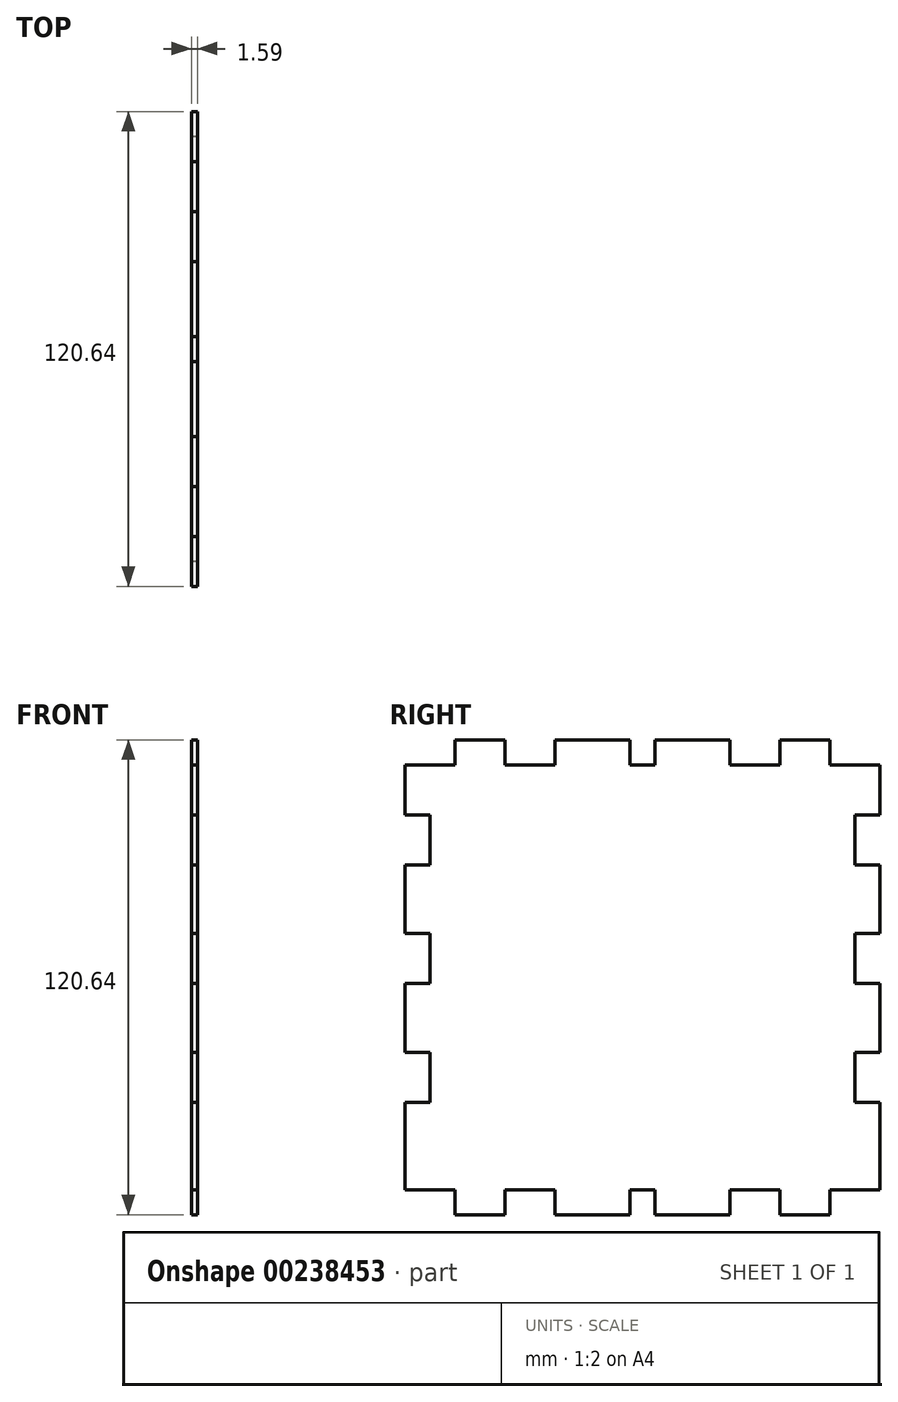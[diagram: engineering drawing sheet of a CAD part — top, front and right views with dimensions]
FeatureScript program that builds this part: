
annotation { "Feature Type Name" : "Feature", "Feature Type Description" : "" }
export const myFeature = defineFeature(function(context is Context, id is Id, definition is map)
    precondition{}
    {
        {
            var Q0;
            Q0=qCreatedBy(makeId("Right.planeOp"),FACE);
            var sketch = newSketch(context, id + "F0", { "sketchPlane" : qUnion([Q0])});
            skLineSegment(sketch, "E0.bottom", {"start": v(60.32, 60.33) * mm, "end": v(-60.33, 60.33) * mm});
            skLineSegment(sketch, "E0.top", {"start": v(60.33, -60.33) * mm, "end": v(-60.32, -60.33) * mm});
            skLineSegment(sketch, "E0.left", {"start": v(60.32, 60.33) * mm, "end": v(60.33, -60.33) * mm});
            skLineSegment(sketch, "E0.right", {"start": v(-60.33, 60.33) * mm, "end": v(-60.32, -60.33) * mm});
            skPoint(sketch, "E0.middle", {"position": v(0, 0) * mm});
            skSolve(sketch);
        }
        {
            var Q0;
            Q0=makeQuery(id+"F0.imprint","IMPRINT",FACE,{"disambiguationData":[TD([[makeQuery(id+"F0.imprint","IMPRINT",EDGE,{"derivedFrom":sQuery(id+"F0.wireOp",EDGE,"E0.bottom")}),1.0]])]});
            extrude(context, id + "F1", {"entities" : qUnion([Q0]), "depth" : 1.59 * mm});
        }
        {
            var Q0;
            Q0=makeQuery(id+"F1.opExtrude","CAP_FACE",FACE,{"disambiguationData":[OSD([sQuery(id+"F0.wireOp",EDGE,"E0.bottom"),sQuery(id+"F0.wireOp",EDGE,"E0.top"),sQuery(id+"F0.wireOp",EDGE,"E0.left"),sQuery(id+"F0.wireOp",EDGE,"E0.right")])],"isStart":true});
            var sketch = newSketch(context, id + "F2", { "sketchPlane" : qUnion([Q0])});
            skLineSegment(sketch, "E1.bottom", {"start": v(60.33, 60.33) * mm, "end": v(47.63, 60.33) * mm});
            skLineSegment(sketch, "E1.top", {"start": v(60.33, 53.98) * mm, "end": v(47.63, 53.98) * mm});
            skLineSegment(sketch, "E1.left", {"start": v(60.33, 60.33) * mm, "end": v(60.33, 53.98) * mm});
            skLineSegment(sketch, "E1.right", {"start": v(47.63, 60.33) * mm, "end": v(47.63, 53.98) * mm});
            skSolve(sketch);
        }
        {
            var Q0;
            Q0=makeQuery(id+"F2.imprint","IMPRINT",FACE,{"disambiguationData":[TD([[makeQuery(id+"F2.imprint","IMPRINT",EDGE,{"derivedFrom":sQuery(id+"F2.wireOp",EDGE,"E1.bottom")}),-1.0]])]});
            extrude(context, id + "F3", {"entities" : qUnion([Q0]), "operationType" : NewBodyOperationType.REMOVE, "oppositeDirection" : true, "depth" : 1.59 * mm});
        }
        {
            var Q0;
            Q0=makeQuery(id+"F1.opExtrude","CAP_FACE",FACE,{"disambiguationData":[OSD([sQuery(id+"F0.wireOp",EDGE,"E0.bottom"),sQuery(id+"F0.wireOp",EDGE,"E0.top"),sQuery(id+"F0.wireOp",EDGE,"E0.left"),sQuery(id+"F0.wireOp",EDGE,"E0.right")])],"isStart":true});
            var sketch = newSketch(context, id + "F4", { "sketchPlane" : qUnion([Q0])});
            skLineSegment(sketch, "E2.bottom", {"start": v(34.93, 60.33) * mm, "end": v(22.23, 60.33) * mm});
            skLineSegment(sketch, "E2.top", {"start": v(34.93, 53.98) * mm, "end": v(22.23, 53.98) * mm});
            skLineSegment(sketch, "E2.left", {"start": v(34.93, 60.33) * mm, "end": v(34.93, 53.98) * mm});
            skLineSegment(sketch, "E2.right", {"start": v(22.23, 60.33) * mm, "end": v(22.23, 53.98) * mm});
            skSolve(sketch);
        }
        {
            var Q0;
            Q0=qSketchRegion(id+"F4",true);
            extrude(context, id + "F5", {"entities" : qUnion([Q0]), "operationType" : NewBodyOperationType.REMOVE, "oppositeDirection" : true, "depth" : 1.59 * mm});
        }
        {
            var Q0;
            Q0=makeQuery(id+"F1.opExtrude","CAP_FACE",FACE,{"disambiguationData":[OSD([sQuery(id+"F0.wireOp",EDGE,"E0.bottom"),sQuery(id+"F0.wireOp",EDGE,"E0.top"),sQuery(id+"F0.wireOp",EDGE,"E0.left"),sQuery(id+"F0.wireOp",EDGE,"E0.right")])],"isStart":true});
            var sketch = newSketch(context, id + "F6", { "sketchPlane" : qUnion([Q0])});
            skLineSegment(sketch, "E3.bottom", {"start": v(3.18, 60.33) * mm, "end": v(-3.17, 60.33) * mm});
            skLineSegment(sketch, "E3.top", {"start": v(3.18, 53.98) * mm, "end": v(-3.17, 53.98) * mm});
            skLineSegment(sketch, "E3.left", {"start": v(3.18, 60.33) * mm, "end": v(3.18, 53.98) * mm});
            skLineSegment(sketch, "E3.right", {"start": v(-3.17, 60.33) * mm, "end": v(-3.17, 53.98) * mm});
            skSolve(sketch);
        }
        {
            var Q0;
            Q0=qSketchRegion(id+"F6",true);
            extrude(context, id + "F7", {"entities" : qUnion([Q0]), "operationType" : NewBodyOperationType.REMOVE, "oppositeDirection" : true, "depth" : 1.59 * mm});
        }
        {
            var Q0;
            Q0=makeQuery(id+"F1.opExtrude","CAP_FACE",FACE,{"disambiguationData":[OSD([sQuery(id+"F0.wireOp",EDGE,"E0.bottom"),sQuery(id+"F0.wireOp",EDGE,"E0.top"),sQuery(id+"F0.wireOp",EDGE,"E0.left"),sQuery(id+"F0.wireOp",EDGE,"E0.right")])],"isStart":true});
            var sketch = newSketch(context, id + "F8", { "sketchPlane" : qUnion([Q0])});
            skLineSegment(sketch, "E4.bottom", {"start": v(-60.32, 60.33) * mm, "end": v(-47.62, 60.33) * mm});
            skLineSegment(sketch, "E4.top", {"start": v(-60.32, 53.98) * mm, "end": v(-47.62, 53.98) * mm});
            skLineSegment(sketch, "E4.left", {"start": v(-60.32, 60.33) * mm, "end": v(-60.32, 53.98) * mm});
            skLineSegment(sketch, "E4.right", {"start": v(-47.62, 60.33) * mm, "end": v(-47.62, 53.98) * mm});
            skSolve(sketch);
        }
        {
            var Q0;
            Q0=makeQuery(id+"F8.imprint","IMPRINT",FACE,{"disambiguationData":[TD([[makeQuery(id+"F8.imprint","IMPRINT",EDGE,{"derivedFrom":sQuery(id+"F8.wireOp",EDGE,"E4.bottom")}),-1.0]])]});
            extrude(context, id + "F9", {"entities" : qUnion([Q0]), "operationType" : NewBodyOperationType.REMOVE, "oppositeDirection" : true, "depth" : 1.59 * mm});
        }
        {
            var Q0;
            Q0=makeQuery(id+"F1.opExtrude","CAP_FACE",FACE,{"disambiguationData":[OSD([sQuery(id+"F0.wireOp",EDGE,"E0.bottom"),sQuery(id+"F0.wireOp",EDGE,"E0.top"),sQuery(id+"F0.wireOp",EDGE,"E0.left"),sQuery(id+"F0.wireOp",EDGE,"E0.right")])],"isStart":true});
            var sketch = newSketch(context, id + "F10", { "sketchPlane" : qUnion([Q0])});
            skLineSegment(sketch, "E5.bottom", {"start": v(-22.22, 60.33) * mm, "end": v(-34.92, 60.33) * mm});
            skLineSegment(sketch, "E5.top", {"start": v(-22.22, 53.98) * mm, "end": v(-34.92, 53.98) * mm});
            skLineSegment(sketch, "E5.left", {"start": v(-22.22, 60.33) * mm, "end": v(-22.22, 53.98) * mm});
            skLineSegment(sketch, "E5.right", {"start": v(-34.92, 60.33) * mm, "end": v(-34.92, 53.98) * mm});
            skSolve(sketch);
        }
        {
            var Q0;
            Q0=makeQuery(id+"F10.imprint","IMPRINT",FACE,{"disambiguationData":[TD([[makeQuery(id+"F10.imprint","IMPRINT",EDGE,{"derivedFrom":sQuery(id+"F10.wireOp",EDGE,"E5.bottom")}),-1.0]])]});
            extrude(context, id + "F11", {"entities" : qUnion([Q0]), "operationType" : NewBodyOperationType.REMOVE, "oppositeDirection" : true, "depth" : 1.59 * mm});
        }
        {
            var Q0;
            Q0=makeQuery(id+"F1.opExtrude","CAP_FACE",FACE,{"disambiguationData":[OSD([sQuery(id+"F0.wireOp",EDGE,"E0.bottom"),sQuery(id+"F0.wireOp",EDGE,"E0.top"),sQuery(id+"F0.wireOp",EDGE,"E0.left"),sQuery(id+"F0.wireOp",EDGE,"E0.right")])],"isStart":true});
            var sketch = newSketch(context, id + "F12", { "sketchPlane" : qUnion([Q0])});
            skLineSegment(sketch, "E6.bottom", {"start": v(-60.32, 41.28) * mm, "end": v(-53.97, 41.28) * mm});
            skLineSegment(sketch, "E6.top", {"start": v(-60.32, 28.58) * mm, "end": v(-53.97, 28.58) * mm});
            skLineSegment(sketch, "E6.left", {"start": v(-60.32, 41.28) * mm, "end": v(-60.32, 28.57) * mm});
            skLineSegment(sketch, "E6.right", {"start": v(-53.97, 41.28) * mm, "end": v(-53.97, 28.58) * mm});
            skSolve(sketch);
        }
        {
            var Q0;
            Q0=makeQuery(id+"F12.imprint","IMPRINT",FACE,{"disambiguationData":[TD([[makeQuery(id+"F12.imprint","IMPRINT",EDGE,{"derivedFrom":sQuery(id+"F12.wireOp",EDGE,"E6.bottom")}),-1.0]])]});
            extrude(context, id + "F13", {"entities" : qUnion([Q0]), "operationType" : NewBodyOperationType.REMOVE, "oppositeDirection" : true, "depth" : 1.59 * mm});
        }
        {
            var Q0;
            Q0=makeQuery(id+"F1.opExtrude","CAP_FACE",FACE,{"disambiguationData":[OSD([sQuery(id+"F0.wireOp",EDGE,"E0.bottom"),sQuery(id+"F0.wireOp",EDGE,"E0.top"),sQuery(id+"F0.wireOp",EDGE,"E0.left"),sQuery(id+"F0.wireOp",EDGE,"E0.right")])],"isStart":true});
            var sketch = newSketch(context, id + "F14", { "sketchPlane" : qUnion([Q0])});
            skLineSegment(sketch, "E7.bottom", {"start": v(-60.32, 11.11) * mm, "end": v(-53.97, 11.11) * mm});
            skLineSegment(sketch, "E7.top", {"start": v(-60.32, -1.59) * mm, "end": v(-53.97, -1.59) * mm});
            skLineSegment(sketch, "E7.left", {"start": v(-60.32, 11.11) * mm, "end": v(-60.32, -1.59) * mm});
            skLineSegment(sketch, "E7.right", {"start": v(-53.97, 11.11) * mm, "end": v(-53.97, -1.59) * mm});
            skSolve(sketch);
        }
        {
            var Q0;
            Q0=makeQuery(id+"F14.imprint","IMPRINT",FACE,{"disambiguationData":[TD([[makeQuery(id+"F14.imprint","IMPRINT",EDGE,{"derivedFrom":sQuery(id+"F14.wireOp",EDGE,"E7.bottom")}),-1.0]])]});
            extrude(context, id + "F15", {"entities" : qUnion([Q0]), "operationType" : NewBodyOperationType.REMOVE, "oppositeDirection" : true, "depth" : 1.59 * mm});
        }
        {
            var Q0;
            Q0=makeQuery(id+"F1.opExtrude","CAP_FACE",FACE,{"disambiguationData":[OSD([sQuery(id+"F0.wireOp",EDGE,"E0.bottom"),sQuery(id+"F0.wireOp",EDGE,"E0.top"),sQuery(id+"F0.wireOp",EDGE,"E0.left"),sQuery(id+"F0.wireOp",EDGE,"E0.right")])],"isStart":true});
            var sketch = newSketch(context, id + "F16", { "sketchPlane" : qUnion([Q0])});
            skLineSegment(sketch, "E8.bottom", {"start": v(-60.33, -19.05) * mm, "end": v(-53.98, -19.05) * mm});
            skLineSegment(sketch, "E8.top", {"start": v(-60.33, -31.75) * mm, "end": v(-53.98, -31.75) * mm});
            skLineSegment(sketch, "E8.left", {"start": v(-60.33, -19.05) * mm, "end": v(-60.33, -31.75) * mm});
            skLineSegment(sketch, "E8.right", {"start": v(-53.98, -19.05) * mm, "end": v(-53.98, -31.75) * mm});
            skSolve(sketch);
        }
        {
            var Q0;
            Q0=makeQuery(id+"F16.imprint","IMPRINT",FACE,{"disambiguationData":[TD([[makeQuery(id+"F16.imprint","IMPRINT",EDGE,{"derivedFrom":sQuery(id+"F16.wireOp",EDGE,"E8.bottom")}),-1.0]])]});
            extrude(context, id + "F17", {"entities" : qUnion([Q0]), "operationType" : NewBodyOperationType.REMOVE, "oppositeDirection" : true, "depth" : 1.59 * mm});
        }
        {
            var Q0;
            Q0=makeQuery(id+"F1.opExtrude","CAP_FACE",FACE,{"disambiguationData":[OSD([sQuery(id+"F0.wireOp",EDGE,"E0.bottom"),sQuery(id+"F0.wireOp",EDGE,"E0.top"),sQuery(id+"F0.wireOp",EDGE,"E0.left"),sQuery(id+"F0.wireOp",EDGE,"E0.right")])],"isStart":true});
            var sketch = newSketch(context, id + "F18", { "sketchPlane" : qUnion([Q0])});
            skLineSegment(sketch, "E9.bottom", {"start": v(-60.33, -53.98) * mm, "end": v(-47.63, -53.98) * mm});
            skLineSegment(sketch, "E9.top", {"start": v(-60.33, -60.33) * mm, "end": v(-47.63, -60.33) * mm});
            skLineSegment(sketch, "E9.left", {"start": v(-60.33, -53.98) * mm, "end": v(-60.33, -60.33) * mm});
            skLineSegment(sketch, "E9.right", {"start": v(-47.63, -53.98) * mm, "end": v(-47.63, -60.33) * mm});
            skLineSegment(sketch, "E10.bottom", {"start": v(60.32, -53.98) * mm, "end": v(47.62, -53.98) * mm});
            skLineSegment(sketch, "E10.top", {"start": v(60.32, -60.33) * mm, "end": v(47.62, -60.33) * mm});
            skLineSegment(sketch, "E10.left", {"start": v(60.32, -53.98) * mm, "end": v(60.32, -60.33) * mm});
            skLineSegment(sketch, "E10.right", {"start": v(47.62, -53.98) * mm, "end": v(47.62, -60.33) * mm});
            skSolve(sketch);
        }
        {
            var Q0;
            Q0=qSketchRegion(id+"F18",true);
            extrude(context, id + "F19", {"entities" : qUnion([Q0]), "operationType" : NewBodyOperationType.REMOVE, "oppositeDirection" : true, "depth" : 1.59 * mm});
        }
        {
            var Q0;
            Q0=makeQuery(id+"F1.opExtrude","CAP_FACE",FACE,{"disambiguationData":[OSD([sQuery(id+"F0.wireOp",EDGE,"E0.bottom"),sQuery(id+"F0.wireOp",EDGE,"E0.top"),sQuery(id+"F0.wireOp",EDGE,"E0.left"),sQuery(id+"F0.wireOp",EDGE,"E0.right")])],"isStart":true});
            var sketch = newSketch(context, id + "F20", { "sketchPlane" : qUnion([Q0])});
            skLineSegment(sketch, "E11.bottom", {"start": v(-34.93, -60.33) * mm, "end": v(-22.23, -60.33) * mm});
            skLineSegment(sketch, "E11.top", {"start": v(-34.93, -53.98) * mm, "end": v(-22.23, -53.98) * mm});
            skLineSegment(sketch, "E11.left", {"start": v(-34.93, -60.33) * mm, "end": v(-34.93, -53.98) * mm});
            skLineSegment(sketch, "E11.right", {"start": v(-22.23, -60.33) * mm, "end": v(-22.23, -53.98) * mm});
            skLineSegment(sketch, "E12.bottom", {"start": v(-3.18, -60.33) * mm, "end": v(3.17, -60.33) * mm});
            skLineSegment(sketch, "E12.top", {"start": v(-3.18, -53.98) * mm, "end": v(3.17, -53.98) * mm});
            skLineSegment(sketch, "E12.left", {"start": v(-3.18, -60.33) * mm, "end": v(-3.18, -53.98) * mm});
            skLineSegment(sketch, "E12.right", {"start": v(3.17, -60.33) * mm, "end": v(3.17, -53.98) * mm});
            skLineSegment(sketch, "E13.bottom", {"start": v(22.22, -60.33) * mm, "end": v(34.92, -60.33) * mm});
            skLineSegment(sketch, "E13.top", {"start": v(22.22, -53.97) * mm, "end": v(34.92, -53.97) * mm});
            skLineSegment(sketch, "E13.left", {"start": v(22.22, -60.33) * mm, "end": v(22.22, -53.97) * mm});
            skLineSegment(sketch, "E13.right", {"start": v(34.92, -60.33) * mm, "end": v(34.92, -53.97) * mm});
            skSolve(sketch);
        }
        {
            var Q0;
            Q0=qSketchRegion(id+"F20",true);
            extrude(context, id + "F21", {"entities" : qUnion([Q0]), "operationType" : NewBodyOperationType.REMOVE, "oppositeDirection" : true, "depth" : 1.59 * mm});
        }
        {
            var Q0;
            Q0=makeQuery(id+"F1.opExtrude","CAP_FACE",FACE,{"disambiguationData":[OSD([sQuery(id+"F0.wireOp",EDGE,"E0.bottom"),sQuery(id+"F0.wireOp",EDGE,"E0.top"),sQuery(id+"F0.wireOp",EDGE,"E0.left"),sQuery(id+"F0.wireOp",EDGE,"E0.right")])],"isStart":true});
            var sketch = newSketch(context, id + "F22", { "sketchPlane" : qUnion([Q0])});
            skLineSegment(sketch, "E14.bottom", {"start": v(60.33, 41.27) * mm, "end": v(53.98, 41.27) * mm});
            skLineSegment(sketch, "E14.top", {"start": v(60.33, 28.57) * mm, "end": v(53.98, 28.57) * mm});
            skLineSegment(sketch, "E14.left", {"start": v(60.33, 41.27) * mm, "end": v(60.33, 28.57) * mm});
            skLineSegment(sketch, "E14.right", {"start": v(53.98, 41.27) * mm, "end": v(53.98, 28.57) * mm});
            skLineSegment(sketch, "E15.bottom", {"start": v(60.33, 11.11) * mm, "end": v(53.98, 11.11) * mm});
            skLineSegment(sketch, "E15.top", {"start": v(60.33, -1.59) * mm, "end": v(53.98, -1.59) * mm});
            skLineSegment(sketch, "E15.left", {"start": v(60.33, 11.11) * mm, "end": v(60.33, -1.59) * mm});
            skLineSegment(sketch, "E15.right", {"start": v(53.98, 11.11) * mm, "end": v(53.98, -1.59) * mm});
            skSolve(sketch);
        }
        {
            var Q0;
            Q0=qSketchRegion(id+"F22",true);
            extrude(context, id + "F23", {"entities" : qUnion([Q0]), "operationType" : NewBodyOperationType.REMOVE, "oppositeDirection" : true, "depth" : 1.59 * mm});
        }
        {
            var Q0;
            Q0=makeQuery(id+"F1.opExtrude","CAP_FACE",FACE,{"disambiguationData":[OSD([sQuery(id+"F0.wireOp",EDGE,"E0.bottom"),sQuery(id+"F0.wireOp",EDGE,"E0.top"),sQuery(id+"F0.wireOp",EDGE,"E0.left"),sQuery(id+"F0.wireOp",EDGE,"E0.right")])],"isStart":true});
            var sketch = newSketch(context, id + "F24", { "sketchPlane" : qUnion([Q0])});
            skLineSegment(sketch, "E16.bottom", {"start": v(60.33, -19.05) * mm, "end": v(53.98, -19.05) * mm});
            skLineSegment(sketch, "E16.top", {"start": v(60.33, -31.75) * mm, "end": v(53.98, -31.75) * mm});
            skLineSegment(sketch, "E16.left", {"start": v(60.33, -19.05) * mm, "end": v(60.33, -31.75) * mm});
            skLineSegment(sketch, "E16.right", {"start": v(53.98, -19.05) * mm, "end": v(53.98, -31.75) * mm});
            skSolve(sketch);
        }
        {
            var Q0;
            Q0=qSketchRegion(id+"F24",true);
            extrude(context, id + "F25", {"entities" : qUnion([Q0]), "operationType" : NewBodyOperationType.REMOVE, "oppositeDirection" : true, "depth" : 1.59 * mm});
        }
    });
